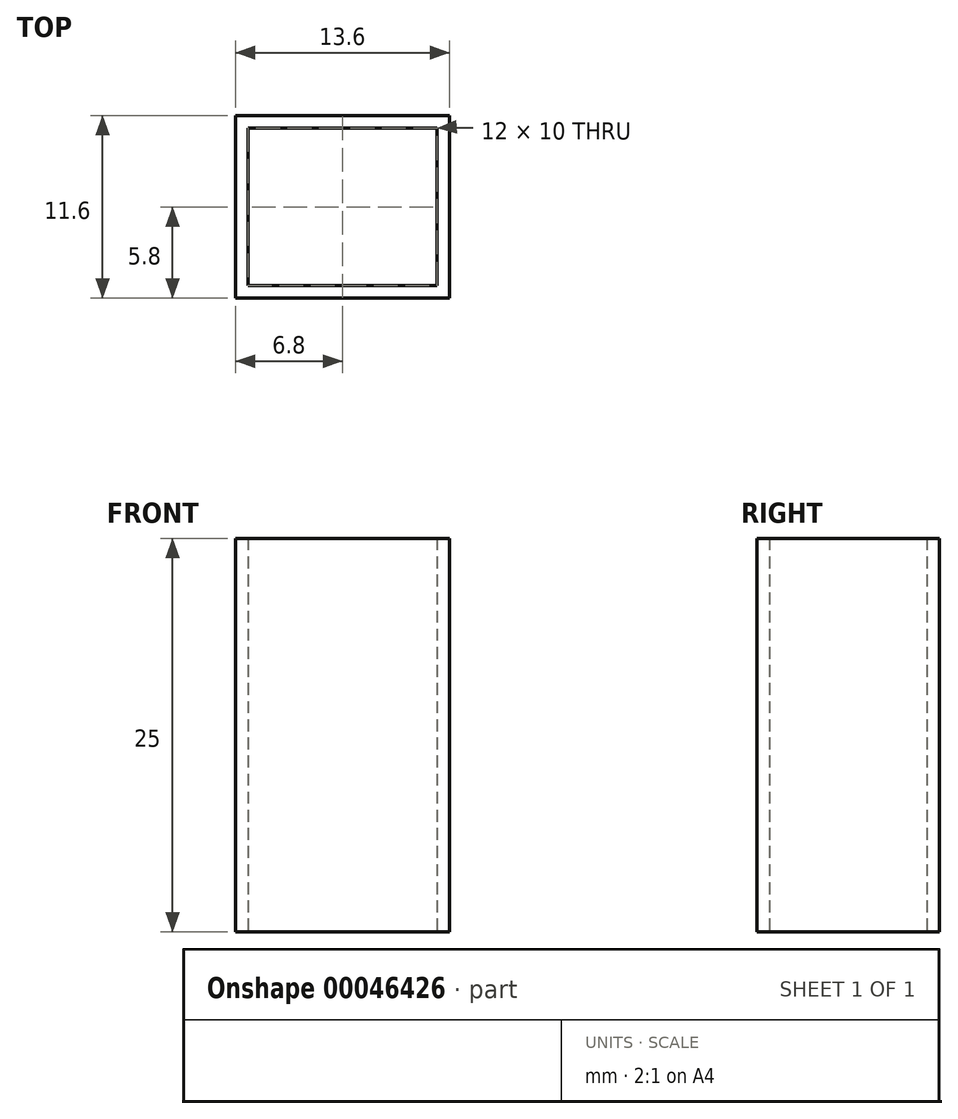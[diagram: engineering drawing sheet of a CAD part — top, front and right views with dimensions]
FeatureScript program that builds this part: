
annotation { "Feature Type Name" : "Feature", "Feature Type Description" : "" }
export const myFeature = defineFeature(function(context is Context, id is Id, definition is map)
    precondition{}
    {
        {
            var Q0;
            Q0=qCreatedBy(makeId("Top.planeOp"),FACE);
            var sketch = newSketch(context, id + "F0", { "sketchPlane" : qUnion([Q0])});
            skLineSegment(sketch, "E0.bottom", {"start": v(6, -5) * mm, "end": v(-6, -5) * mm});
            skLineSegment(sketch, "E0.top", {"start": v(6, 5) * mm, "end": v(-6, 5) * mm});
            skLineSegment(sketch, "E0.left", {"start": v(6, -5) * mm, "end": v(6, 5) * mm});
            skLineSegment(sketch, "E0.right", {"start": v(-6, -5) * mm, "end": v(-6, 5) * mm});
            skPoint(sketch, "E0.middle", {"position": v(0, 0) * mm});
            skLineSegment(sketch, "E1.0", {"start": v(6.8, -5.8) * mm, "end": v(-6.8, -5.8) * mm});
            skLineSegment(sketch, "E1.1", {"start": v(6.8, -5.8) * mm, "end": v(6.8, 5.8) * mm});
            skLineSegment(sketch, "E1.2", {"start": v(6.8, 5.8) * mm, "end": v(-6.8, 5.8) * mm});
            skLineSegment(sketch, "E1.3", {"start": v(-6.8, -5.8) * mm, "end": v(-6.8, 5.8) * mm});
            skSolve(sketch);
        }
        {
            var Q0;
            Q0=makeQuery(id+"F0.imprint","IMPRINT",FACE,{"disambiguationData":[TD([[makeQuery(id+"F0.imprint","IMPRINT",EDGE,{"derivedFrom":sQuery(id+"F0.wireOp",EDGE,"E0.bottom")}),1.0]])]});
            extrude(context, id + "F1", {"entities" : qUnion([Q0]), "depth" : 25 * mm, "offsetDistance" : 25 * mm});
        }
    });
